# Revit family: Practibox_S_cofrecito_empotrado_12_módulos_réf_135001_a_135174
name_source: partatom
category: Equipement électrique
revit_build: Autodesk Revit 2018 (Build: 20170223_1515(x64)
units: mm (PartAtom-declared; Revit-internal decimal feet)

## family parameters
Basée sur le plan de construction = Non
Configuration du panneau = Deux colonnes, circuits au sein
Cote de connecteur circulaire = Utiliser le diamètre
Couper avec des vides une fois chargée = Non
Numéro OmniClass = 23.80.30.11.17
Partagée = Non
Point de calcul de pièce = Non
Titre OmniClass = Distribution Boards and Control Panels
Toujours verticalement = Oui
Type d'élément = Tableau de raccordement

## types (32) — shared parameters
Condiciones Generales de Uso = https://export.legrand.com
Fabricant = "Legrand"
URL = www.legrand.com
anchura = 328 mm  [stored 1.07612 ft]

## per-type parameters (varying)
| type | 1R | 2R | 3R | 4R | Altura | Bornas N | Bornas T | Ina | profundidad | puerta B 1 r | puerta B 2 r | puerta B 3 r | puerta B 4 r | puerta T 1 r | puerta T 2 r | puerta T 3 r | puerta T 4 r | puerta blanca | puerta transparencia | tamaño |
| Practibox_S_cofrecito_empotrado_12_módulos_135021 | Oui | Non | Non | Non | 235 mm  [stored 0.770997 ft] |  |  | 63 A | 102 mm | Oui | Non | Non | Non | Non | Non | Non | Non | Oui | Non | 1 fila |
| Practibox_S_cofrecito_empotrado_24_módulos_135022 | Non | Oui | Non | Non | 385 mm  [stored 1.26312 ft] |  |  | 90 A | 103 mm  [stored 0.337927 ft] | Non | Oui | Non | Non | Non | Non | Non | Non | Oui | Non | 2 fila |
| Practibox_S_cofrecito_empotrado_36_módulos_135023 | Non | Non | Oui | Non | 535 mm  [stored 1.75525 ft] |  |  | 90 A | 103 mm  [stored 0.337927 ft] | Non | Non | Oui | Non | Non | Non | Non | Non | Oui | Non | 3 fila |
| Practibox_S_cofrecito_empotrado_48_módulos_135024 | Non | Non | Non | Oui | 765 mm  [stored 2.50984 ft] |  |  | 90 A | 103 mm  [stored 0.337927 ft] | Non | Non | Non | Oui | Non | Non | Non | Non | Oui | Non | 4 fila |
| Practibox_S_cofrecito_empotrado_12_módulos_135031 | Oui | Non | Non | Non | 235 mm  [stored 0.770997 ft] |  |  | 63 A | 102 mm | Non | Non | Non | Non | Oui | Non | Non | Non | Non | Oui | 1 fila |
| Practibox_S_cofrecito_empotrado_12_módulos_135161 | Oui | Non | Non | Non | 235 mm  [stored 0.770997 ft] | 24 salidas Icc 6kA | 24 salidas Icc 6kA | 63 A | 102 mm | Oui | Non | Non | Non | Non | Non | Non | Non | Oui | Non | 1 fila |
| Practibox_S_cofrecito_empotrado_12_módulos_135171 | Oui | Non | Non | Non | 235 mm  [stored 0.770997 ft] | 24 salidas Icc 6kA | 24 salidas Icc 6kA | 63 A | 102 mm | Non | Non | Non | Non | Oui | Non | Non | Non | Non | Oui | 1 fila |
| Practibox_S_cofrecito_empotrado_12_módulos_135151 | Oui | Non | Non | Non | 235 mm  [stored 0.770997 ft] | 24 salidas Icc 6kA | 24 salidas Icc 6kA | 63 A | 102 mm | Non | Non | Non | Non | Oui | Non | Non | Non | Non | Oui | 1 fila |
| Practibox_S_cofrecito_empotrado_12_módulos_135141 | Oui | Non | Non | Non | 235 mm  [stored 0.770997 ft] | 24 salidas Icc 6kA | 24 salidas Icc 6kA | 63 A | 102 mm | Oui | Non | Non | Non | Non | Non | Non | Non | Oui | Non | 1 fila |
| Practibox_S_cofrecito_empotrado_24_módulos_135032 | Non | Oui | Non | Non | 385 mm  [stored 1.26312 ft] |  |  | 90 A | 103 mm  [stored 0.337927 ft] | Non | Non | Non | Non | Non | Oui | Non | Non | Non | Oui | 2 fila |
| Practibox_S_cofrecito_empotrado_24_módulos_135162 | Non | Oui | Non | Non | 385 mm  [stored 1.26312 ft] | 24 salidas Icc 6kA | 24 salidas Icc 6kA | 90 A | 103 mm  [stored 0.337927 ft] | Non | Oui | Non | Non | Non | Non | Non | Non | Oui | Non | 2 fila |
| Practibox_S_cofrecito_empotrado_24_módulos_135172 | Non | Oui | Non | Non | 385 mm  [stored 1.26312 ft] | 24 salidas Icc 6kA | 24 salidas Icc 6kA | 90 A | 103 mm  [stored 0.337927 ft] | Non | Non | Non | Non | Non | Oui | Non | Non | Non | Oui | 2 fila |
| Practibox_S_cofrecito_empotrado_24_módulos_135142 | Non | Oui | Non | Non | 385 mm  [stored 1.26312 ft] | 24 salidas Icc 6kA | 24 salidas Icc 6kA | 90 A | 103 mm  [stored 0.337927 ft] | Non | Oui | Non | Non | Non | Non | Non | Non | Oui | Non | 2 fila |
| Practibox_S_cofrecito_empotrado_24_módulos_135002 | Non | Oui | Non | Non | 385 mm  [stored 1.26312 ft] |  |  | 90 A | 103 mm  [stored 0.337927 ft] | Non | Oui | Non | Non | Non | Non | Non | Non | Oui | Non | 2 fila |
| Practibox_S_cofrecito_empotrado_24_módulos_135012 | Non | Oui | Non | Non | 385 mm  [stored 1.26312 ft] |  |  | 90 A | 103 mm  [stored 0.337927 ft] | Non | Non | Non | Non | Non | Oui | Non | Non | Non | Oui | 2 fila |
| Practibox_S_cofrecito_empotrado_36_módulos_135033 | Non | Non | Oui | Non | 535 mm  [stored 1.75525 ft] |  |  | 90 A | 103 mm  [stored 0.337927 ft] | Non | Non | Non | Non | Non | Non | Oui | Non | Non | Oui | 3 fila |
| Practibox_S_cofrecito_empotrado_36_módulos_135173 | Non | Non | Oui | Non | 535 mm  [stored 1.75525 ft] | 24 salidas Icc 6kA | 24 salidas Icc 6kA | 90 A | 103 mm  [stored 0.337927 ft] | Non | Non | Non | Non | Non | Non | Oui | Non | Non | Oui | 3 fila |
| Practibox_S_cofrecito_empotrado_36_módulos_135163 | Non | Non | Oui | Non | 535 mm  [stored 1.75525 ft] | 24 salidas Icc 6kA | 24 salidas Icc 6kA | 90 A | 103 mm  [stored 0.337927 ft] | Non | Non | Oui | Non | Non | Non | Non | Non | Oui | Non | 3 fila |
| Practibox_S_cofrecito_empotrado_36_módulos_135143 | Non | Non | Oui | Non | 535 mm  [stored 1.75525 ft] | 24 salidas Icc 6kA | 24 salidas Icc 6kA | 90 A | 103 mm  [stored 0.337927 ft] | Non | Non | Oui | Non | Non | Non | Non | Non | Oui | Non | 3 fila |
| Practibox_S_cofrecito_empotrado_36_módulos_135153 | Non | Non | Oui | Non | 535 mm  [stored 1.75525 ft] | 24 salidas Icc 6kA | 24 salidas Icc 6kA | 90 A | 103 mm  [stored 0.337927 ft] | Non | Non | Non | Non | Non | Non | Oui | Non | Non | Oui | 3 fila |
| Practibox_S_cofrecito_empotrado_36_módulos_135013 | Non | Non | Oui | Non | 535 mm  [stored 1.75525 ft] |  |  | 90 A | 103 mm  [stored 0.337927 ft] | Non | Non | Non | Non | Non | Non | Oui | Non | Non | Oui | 3 fila |
| Practibox_S_cofrecito_empotrado_36_módulos_135003 | Non | Non | Oui | Non | 535 mm  [stored 1.75525 ft] |  |  | 90 A | 103 mm  [stored 0.337927 ft] | Non | Non | Oui | Non | Non | Non | Non | Non | Oui | Non | 3 fila |
| Practibox_S_cofrecito_empotrado_48_módulos_135034 | Non | Non | Non | Oui | 765 mm  [stored 2.50984 ft] |  |  | 90 A | 103 mm  [stored 0.337927 ft] | Non | Non | Non | Non | Non | Non | Non | Oui | Non | Oui | 4 fila |
| Practibox_S_cofrecito_empotrado_48_módulos_135174 | Non | Non | Non | Oui | 765 mm  [stored 2.50984 ft] | 24 salidas Icc 6kA | 24 salidas Icc 6kA | 90 A | 103 mm  [stored 0.337927 ft] | Non | Non | Non | Non | Non | Non | Non | Oui | Non | Oui | 4 fila |
| Practibox_S_cofrecito_empotrado_48_módulos_135164 | Non | Non | Non | Oui | 765 mm  [stored 2.50984 ft] | 24 salidas Icc 6kA | 24 salidas Icc 6kA | 90 A | 103 mm  [stored 0.337927 ft] | Non | Non | Non | Oui | Non | Non | Non | Non | Oui | Non | 4 fila |
| Practibox_S_cofrecito_empotrado_48_módulos_135144 | Non | Non | Non | Oui | 765 mm  [stored 2.50984 ft] | 24 salidas Icc 6kA | 24 salidas Icc 6kA | 90 A | 103 mm  [stored 0.337927 ft] | Non | Non | Non | Oui | Non | Non | Non | Non | Oui | Non | 4 fila |
| Practibox_S_cofrecito_empotrado_48_módulos_135154 | Non | Non | Non | Oui | 765 mm  [stored 2.50984 ft] | 24 salidas Icc 6kA | 24 salidas Icc 6kA | 90 A | 103 mm  [stored 0.337927 ft] | Non | Non | Non | Non | Non | Non | Non | Oui | Non | Oui | 4 fila |
| Practibox_S_cofrecito_empotrado_48_módulos_135004 | Non | Non | Non | Oui | 765 mm  [stored 2.50984 ft] |  |  | 90 A | 103 mm  [stored 0.337927 ft] | Non | Non | Non | Oui | Non | Non | Non | Non | Oui | Non | 4 fila |
| Practibox_S_cofrecito_empotrado_48_módulos_135014 | Non | Non | Non | Oui | 765 mm  [stored 2.50984 ft] |  |  | 90 A | 103 mm  [stored 0.337927 ft] | Non | Non | Non | Non | Non | Non | Non | Oui | Non | Oui | 4 fila |
| Practibox_S_cofrecito_empotrado_24_módulos_135152 | Non | Oui | Non | Non | 385 mm  [stored 1.26312 ft] | 24 salidas Icc 6kA | 24 salidas Icc 6kA | 90 A | 103 mm  [stored 0.337927 ft] | Non | Non | Non | Non | Non | Oui | Non | Non | Non | Oui | 2 fila |
| Practibox_S_cofrecito_empotrado_12_módulos_135001 | Oui | Non | Non | Non | 235 mm  [stored 0.770997 ft] |  |  | 63 A | 102 mm | Oui | Non | Non | Non | Non | Non | Non | Non | Oui | Non | 1 fila |
| Practibox_S_cofrecito_empotrado_12_módulos_135011 | Oui | Non | Non | Non | 235 mm  [stored 0.770997 ft] |  |  | 63 A | 102 mm | Non | Non | Non | Non | Oui | Non | Non | Non | Non | Oui | 1 fila |

note: column(s) folded — value = type name in every type: Description

note: [stored X ft] marks values corroborated as IEEE doubles in the binary element streams (Revit-internal decimal feet)
